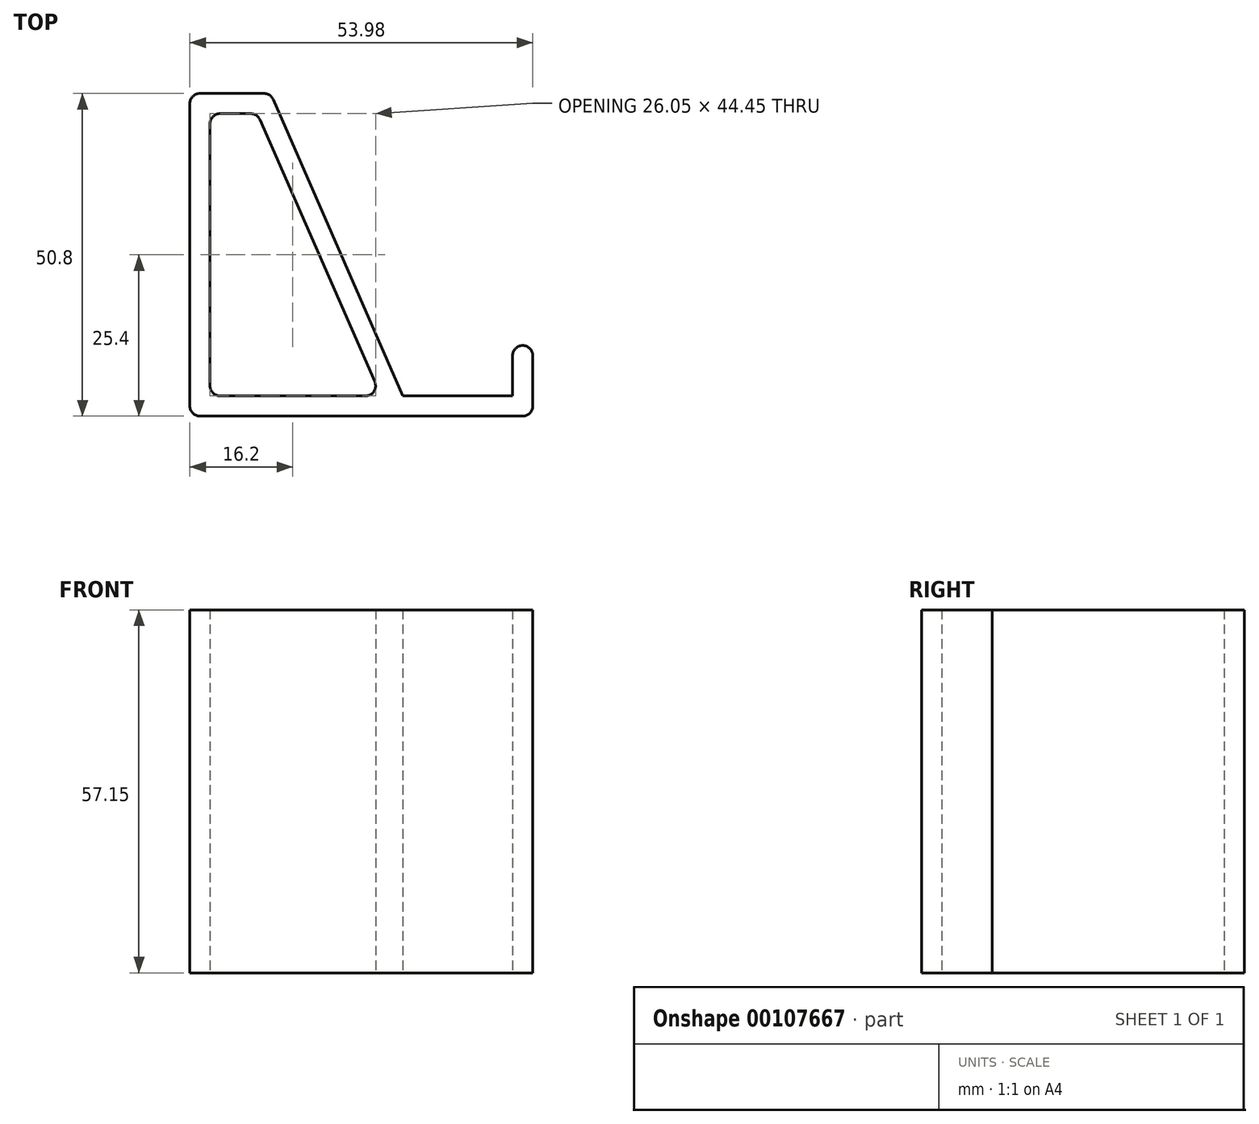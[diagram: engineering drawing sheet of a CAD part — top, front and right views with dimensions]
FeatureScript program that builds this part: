
annotation { "Feature Type Name" : "Feature", "Feature Type Description" : "" }
export const myFeature = defineFeature(function(context is Context, id is Id, definition is map)
    precondition{}
    {
        {
            var Q0;
            Q0=qCreatedBy(makeId("Top.planeOp"),FACE);
            var sketch = newSketch(context, id + "F0", { "sketchPlane" : qUnion([Q0])});
            skLineSegment(sketch, "E0", {"start": v(1.59, 0) * mm, "end": v(34.92, 0) * mm});
            skLineSegment(sketch, "E1", {"start": v(53.98, 1.59) * mm, "end": v(53.98, 9.53) * mm});
            skLineSegment(sketch, "E2", {"start": v(0, 1.59) * mm, "end": v(0, 49.21) * mm});
            skLineSegment(sketch, "E3", {"start": v(1.59, 50.8) * mm, "end": v(11.66, 50.8) * mm});
            skLineSegment(sketch, "E4", {"start": v(13.12, 49.85) * mm, "end": v(34.93, 0) * mm});
            skLineSegment(sketch, "E5", {"start": v(34.92, 0) * mm, "end": v(52.39, 0) * mm});
            skLineSegment(sketch, "E6.0", {"start": v(3.18, 4.76) * mm, "end": v(3.18, 46.04) * mm});
            skLineSegment(sketch, "E6.1", {"start": v(4.76, 3.18) * mm, "end": v(27.64, 3.18) * mm});
            skLineSegment(sketch, "E6.2", {"start": v(11.04, 46.67) * mm, "end": v(29.1, 5.4) * mm});
            skLineSegment(sketch, "E6.3", {"start": v(4.76, 47.63) * mm, "end": v(9.59, 47.63) * mm});
            skLineSegment(sketch, "E7.0", {"start": v(50.8, 3.18) * mm, "end": v(50.8, 9.53) * mm});
            skLineSegment(sketch, "E7.1", {"start": v(33.54, 3.18) * mm, "end": v(50.8, 3.18) * mm});
            skLineSegment(sketch, "E8", {"start": v(52.39, 11.11) * mm, "end": v(52.39, 11.11) * mm});
            skPoint(sketch, "E9.visualSharp", {"position": v(0, 50.8) * mm});
            skArc(sketch, "E9.filletArc", {"start": v(1.59, 50.8) * mm, "mid": v(0.46, 50.34) * mm, "end": v(0, 49.21) * mm});
            skPoint(sketch, "E10.visualSharp", {"position": v(0, 0) * mm});
            skArc(sketch, "E10.filletArc", {"start": v(0, 1.59) * mm, "mid": v(0.46, 0.46) * mm, "end": v(1.59, 0) * mm});
            skPoint(sketch, "E11.visualSharp", {"position": v(3.18, 3.18) * mm});
            skArc(sketch, "E11.filletArc", {"start": v(3.18, 4.76) * mm, "mid": v(3.64, 3.64) * mm, "end": v(4.76, 3.17) * mm});
            skPoint(sketch, "E12.visualSharp", {"position": v(30.07, 3.18) * mm});
            skArc(sketch, "E12.filletArc", {"start": v(27.64, 3.17) * mm, "mid": v(28.97, 3.9) * mm, "end": v(29.1, 5.4) * mm});
            skPoint(sketch, "E13.visualSharp", {"position": v(10.62, 47.63) * mm});
            skArc(sketch, "E13.filletArc", {"start": v(11.04, 46.67) * mm, "mid": v(10.45, 47.37) * mm, "end": v(9.59, 47.63) * mm});
            skPoint(sketch, "E14.visualSharp", {"position": v(12.7, 50.8) * mm});
            skArc(sketch, "E14.filletArc", {"start": v(13.12, 49.85) * mm, "mid": v(12.53, 50.54) * mm, "end": v(11.66, 50.8) * mm});
            skPoint(sketch, "E15.visualSharp", {"position": v(53.98, 0) * mm});
            skArc(sketch, "E15.filletArc", {"start": v(52.39, 0) * mm, "mid": v(53.51, 0.46) * mm, "end": v(53.98, 1.59) * mm});
            skPoint(sketch, "E16.visualSharp", {"position": v(3.18, 47.63) * mm});
            skArc(sketch, "E16.filletArc", {"start": v(4.76, 47.63) * mm, "mid": v(3.64, 47.16) * mm, "end": v(3.17, 46.04) * mm});
            skPoint(sketch, "E17.visualSharp", {"position": v(53.98, 11.11) * mm});
            skArc(sketch, "E17.filletArc", {"start": v(53.98, 9.53) * mm, "mid": v(53.51, 10.65) * mm, "end": v(52.39, 11.11) * mm});
            skPoint(sketch, "E18.visualSharp", {"position": v(50.8, 11.11) * mm});
            skArc(sketch, "E18.filletArc", {"start": v(52.39, 11.11) * mm, "mid": v(51.26, 10.65) * mm, "end": v(50.8, 9.53) * mm});
            skSolve(sketch);
        }
        {
            var Q0;
            {var subQ0=sQuery(id+"F0.wireOp",EDGE,"E0");Q0=makeQuery(id+"F0.imprint","IMPRINT",FACE,{"disambiguationData":[TD([[makeQuery(id+"F0.imprint","IMPRINT",EDGE,{"derivedFrom":subQ0}),1.0]])]});}
            var Q1;
            Q1=makeQuery(id+"F0.imprint","IMPRINT",FACE,{"disambiguationData":[TD([[makeQuery(id+"F0.imprint","IMPRINT",EDGE,{"derivedFrom":sQuery(id+"F0.wireOp",EDGE,"E1")}),1.0]])]});
            extrude(context, id + "F1", {"entities" : qUnion([Q0, Q1]), "depth" : 57.15 * mm});
        }
    });
